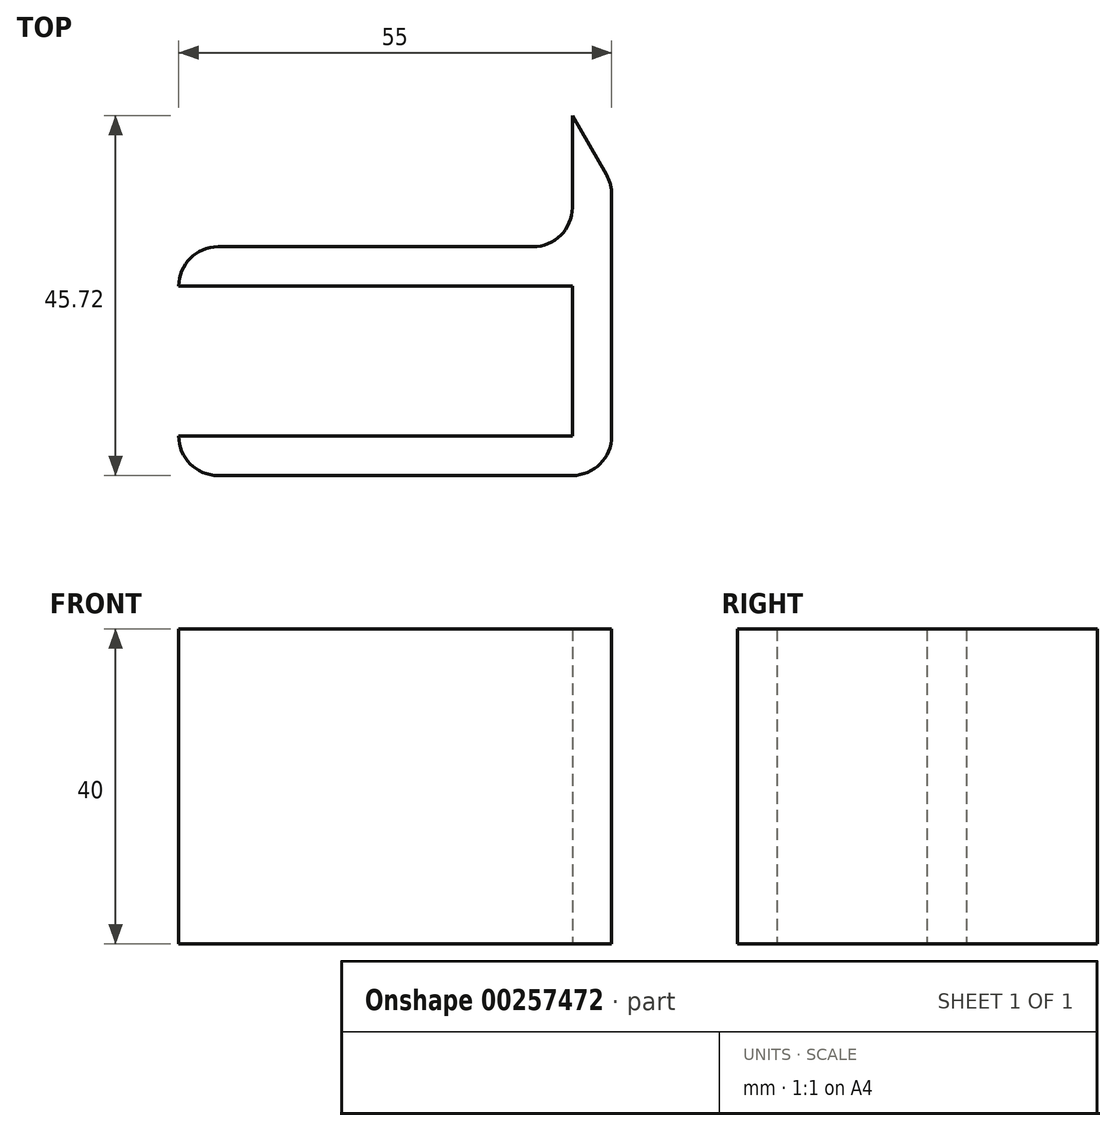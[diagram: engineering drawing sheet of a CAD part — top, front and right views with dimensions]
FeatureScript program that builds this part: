
annotation { "Feature Type Name" : "Feature", "Feature Type Description" : "" }
export const myFeature = defineFeature(function(context is Context, id is Id, definition is map)
    precondition{}
    {
        {
            var Q0;
            Q0=qCreatedBy(makeId("Top.planeOp"),FACE);
            var sketch = newSketch(context, id + "F0", { "sketchPlane" : qUnion([Q0])});
            skLineSegment(sketch, "E0.bottom", {"start": v(27.5, -14.53) * mm, "end": v(-27.5, -14.53) * mm});
            skLineSegment(sketch, "E0.top", {"start": v(22.5, 14.53) * mm, "end": v(-27.5, 14.53) * mm});
            skLineSegment(sketch, "E0.left", {"start": v(27.5, -14.53) * mm, "end": v(27.5, 14.53) * mm});
            skLineSegment(sketch, "E0.right", {"start": v(-27.5, -14.53) * mm, "end": v(-27.5, -9.52) * mm});
            skPoint(sketch, "E0.middle", {"position": v(0, 0) * mm});
            skLineSegment(sketch, "E1.bottom", {"start": v(-27.5, 9.53) * mm, "end": v(22.5, 9.53) * mm});
            skLineSegment(sketch, "E1.top", {"start": v(-27.5, -9.52) * mm, "end": v(22.5, -9.52) * mm});
            skLineSegment(sketch, "E1.right", {"start": v(22.5, 9.53) * mm, "end": v(22.5, -9.53) * mm});
            skLineSegment(sketch, "E2.trimOffspring", {"start": v(-27.5, 9.53) * mm, "end": v(-27.5, 14.53) * mm});
            skLineSegment(sketch, "E3.right", {"start": v(22.5, 14.53) * mm, "end": v(22.5, 22.53) * mm});
            skLineSegment(sketch, "E4", {"start": v(27.5, 14.53) * mm, "end": v(27.5, 22.53) * mm});
            skLineSegment(sketch, "E5", {"start": v(27.5, 22.53) * mm, "end": v(22.5, 31.19) * mm});
            skLineSegment(sketch, "E6", {"start": v(22.5, 22.53) * mm, "end": v(22.5, 31.19) * mm});
            skSolve(sketch);
        }
        {
            var Q0;
            Q0 = qSketchRegion(id + "F0", true);
            extrude(context, id + "F1", {"entities" : qUnion([Q0]), "depth" : 40 * mm});
        }
        {
            var Q0;
            Q0=makeQuery(id+"F1.opExtrude","SWEPT_EDGE",EDGE,{"disambiguationData":[OSD([sQuery(id+"F0.wireOp",EDGE,"E0.top"),sQuery(id+"F0.wireOp",EDGE,"E2.trimOffspring")])]});
            var Q1;
            Q1=makeQuery(id+"F1.opExtrude","SWEPT_EDGE",EDGE,{"disambiguationData":[OSD([sQuery(id+"F0.wireOp",EDGE,"E0.bottom"),sQuery(id+"F0.wireOp",EDGE,"E0.right")])]});
            var Q2;
            Q2=makeQuery(id+"F1.opExtrude","SWEPT_EDGE",EDGE,{"disambiguationData":[OSD([sQuery(id+"F0.wireOp",EDGE,"E0.bottom"),sQuery(id+"F0.wireOp",EDGE,"E0.left")])]});
            var Q3;
            Q3=makeQuery(id+"F1.opExtrude","SWEPT_EDGE",EDGE,{"disambiguationData":[OSD([sQuery(id+"F0.wireOp",EDGE,"E4"),sQuery(id+"F0.wireOp",EDGE,"E5")])]});
            var Q4;
            Q4=makeQuery(id+"F1.opExtrude","SWEPT_EDGE",EDGE,{"disambiguationData":[OSD([sQuery(id+"F0.wireOp",EDGE,"E0.top"),sQuery(id+"F0.wireOp",EDGE,"E3.right")])]});
            fillet(context, id + "F2", {"entities" : qUnion([Q0, Q1, Q2, Q3, Q4]), "radius" : 5 * mm, "tangentPropagation" : true, "allowEdgeOverflow" : false});
        }
    });
